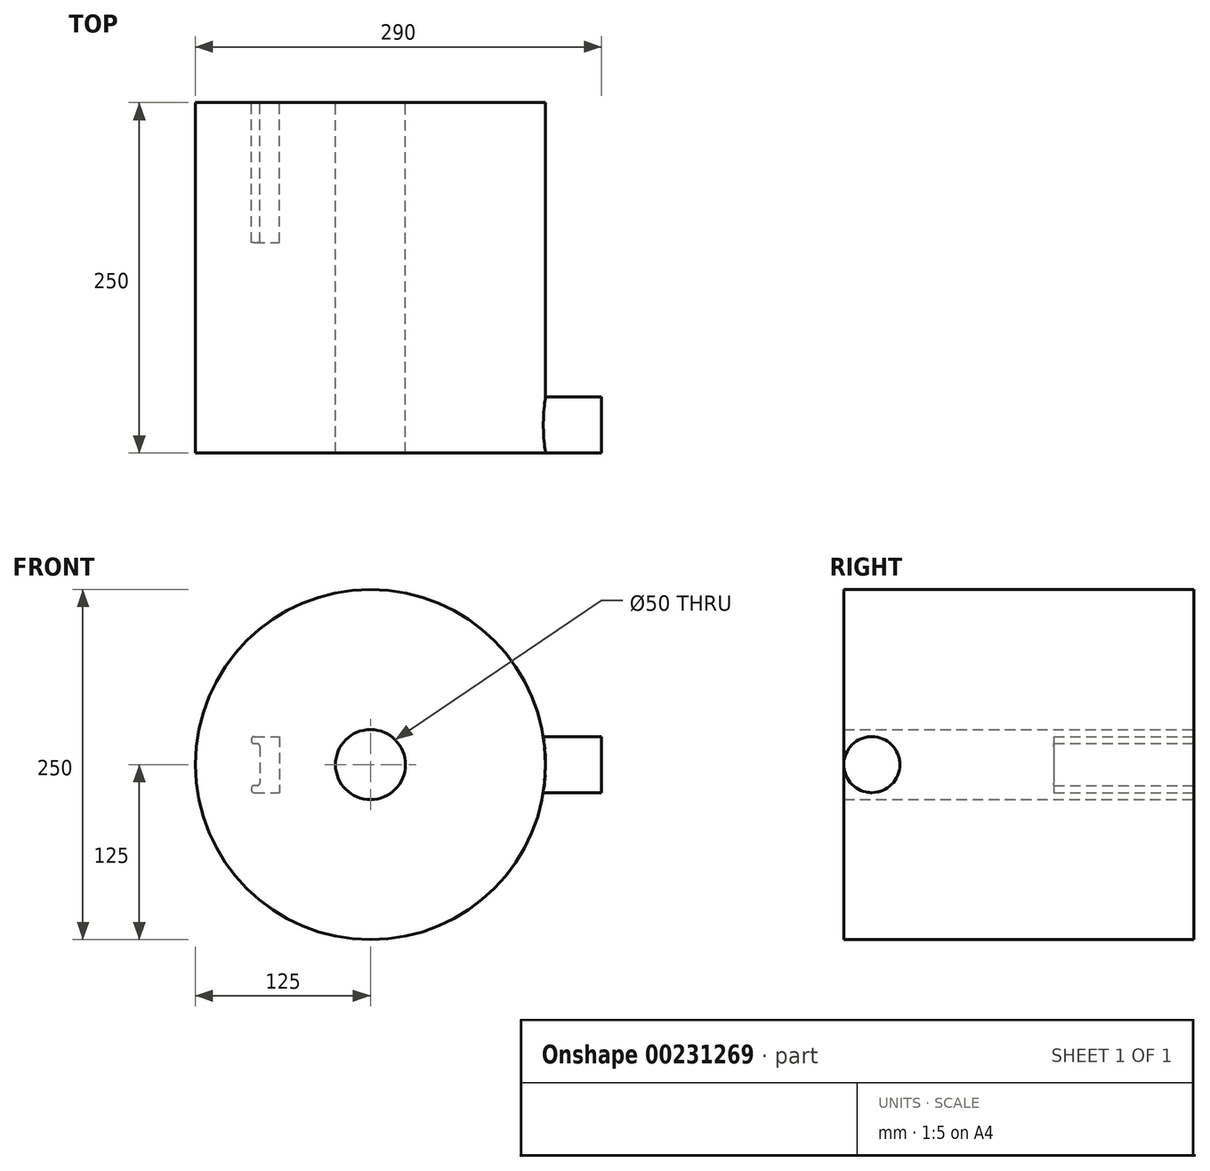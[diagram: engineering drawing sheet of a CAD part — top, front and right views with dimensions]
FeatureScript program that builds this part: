
annotation { "Feature Type Name" : "Feature", "Feature Type Description" : "" }
export const myFeature = defineFeature(function(context is Context, id is Id, definition is map)
    precondition{}
    {
        {
            var Q0;
            Q0=qCreatedBy(makeId("Front.planeOp"),FACE);
            var sketch = newSketch(context, id + "F0", { "sketchPlane" : qUnion([Q0])});
            skCircle(sketch, "E0", {"center": v(0, 0) * mm, "radius": 25 * mm});
            skCircle(sketch, "E1", {"center": v(0, 0) * mm, "radius": 125 * mm});
            skSolve(sketch);
        }
        {
            var Q0;
            Q0=makeQuery(id+"F0.imprint","IMPRINT",FACE,{"disambiguationData":[TD([[makeQuery(id+"F0.imprint","IMPRINT",EDGE,{"derivedFrom":sQuery(id+"F0.wireOp",EDGE,"E0")}),-1.0]])]});
            extrude(context, id + "F1", {"entities" : qUnion([Q0]), "depth" : 250 * mm});
        }
        {
            var Q0;
            Q0=qCreatedBy(makeId("Front.planeOp"),FACE);
            var sketch = newSketch(context, id + "F2", { "sketchPlane" : qUnion([Q0])});
            skLineSegment(sketch, "E2.bottom", {"start": v(-83, 20) * mm, "end": v(-65, 20) * mm});
            skLineSegment(sketch, "E2.top", {"start": v(-83, -20) * mm, "end": v(-65, -20) * mm});
            skLineSegment(sketch, "E2.left", {"start": v(-85, 18) * mm, "end": v(-85, 17) * mm});
            skLineSegment(sketch, "E2.right", {"start": v(-65, 20) * mm, "end": v(-65, -20) * mm});
            skPoint(sketch, "E2.middle", {"position": v(-75, 0) * mm});
            skLineSegment(sketch, "E3", {"start": v(-83, 15) * mm, "end": v(-81, 15) * mm});
            skLineSegment(sketch, "E4", {"start": v(-79, 13) * mm, "end": v(-79, -13) * mm});
            skLineSegment(sketch, "E5", {"start": v(-81, -15) * mm, "end": v(-83, -15) * mm});
            skLineSegment(sketch, "E6.trimOffspring", {"start": v(-85, -17) * mm, "end": v(-85, -18) * mm});
            skPoint(sketch, "E7.visualSharp", {"position": v(-85, 15) * mm});
            skArc(sketch, "E7.filletArc", {"start": v(-85, 17) * mm, "mid": v(-84.41, 15.59) * mm, "end": v(-83, 15) * mm});
            skPoint(sketch, "E8.visualSharp", {"position": v(-85, -15) * mm});
            skArc(sketch, "E8.filletArc", {"start": v(-83, -15) * mm, "mid": v(-84.41, -15.59) * mm, "end": v(-85, -17) * mm});
            skPoint(sketch, "E9.visualSharp", {"position": v(-85, 20) * mm});
            skArc(sketch, "E9.filletArc", {"start": v(-83, 20) * mm, "mid": v(-84.41, 19.41) * mm, "end": v(-85, 18) * mm});
            skPoint(sketch, "E10.visualSharp", {"position": v(-85, -20) * mm});
            skArc(sketch, "E10.filletArc", {"start": v(-85, -18) * mm, "mid": v(-84.41, -19.41) * mm, "end": v(-83, -20) * mm});
            skPoint(sketch, "E11.visualSharp", {"position": v(-79, 15) * mm});
            skArc(sketch, "E11.filletArc", {"start": v(-79, 13) * mm, "mid": v(-79.59, 14.41) * mm, "end": v(-81, 15) * mm});
            skPoint(sketch, "E12.visualSharp", {"position": v(-79, -15) * mm});
            skArc(sketch, "E12.filletArc", {"start": v(-81, -15) * mm, "mid": v(-79.59, -14.41) * mm, "end": v(-79, -13) * mm});
            skSolve(sketch);
        }
        {
            var Q0;
            Q0=makeQuery(id+"F2.imprint","IMPRINT",FACE,{"disambiguationData":[TD([[makeQuery(id+"F2.imprint","IMPRINT",EDGE,{"derivedFrom":sQuery(id+"F2.wireOp",EDGE,"E2.bottom")}),-1.0]])]});
            extrude(context, id + "F3", {"entities" : qUnion([Q0]), "operationType" : NewBodyOperationType.REMOVE, "depth" : 100 * mm});
        }
        {
            var Q0;
            Q0=qCreatedBy(makeId("Right.planeOp"),FACE);
            cPlane(context, id + "F4", {"entities" : qUnion([Q0]), "cplaneType" : CPlaneType.OFFSET, "offset" : 125 * mm, "width" : 150 * mm, "height" : 150 * mm});
        }
        {
            var Q0;
            Q0=qCreatedBy(id+"F4.planeOp",FACE);
            var sketch = newSketch(context, id + "F5", { "sketchPlane" : qUnion([Q0])});
            skCircle(sketch, "E13", {"center": v(-230, 0) * mm, "radius": 20 * mm});
            skLineSegment(sketch, "E14.0", {"start": v(-250, -125) * mm, "end": v(-250, 125) * mm, "construction": true});
            skSolve(sketch);
        }
        {
            var Q0;
            Q0=makeQuery(id+"F5.imprint","IMPRINT",FACE,{"disambiguationData":[TD([[makeQuery(id+"F5.imprint","IMPRINT",EDGE,{"derivedFrom":sQuery(id+"F5.wireOp",EDGE,"E13")}),1.0]])]});
            extrude(context, id + "F6", {"entities" : qUnion([Q0]), "operationType" : NewBodyOperationType.ADD, "depth" : 40 * mm, "hasSecondDirection" : true, "secondDirectionOppositeDirection" : true, "secondDirectionDepth" : 10 * mm});
        }
    });
